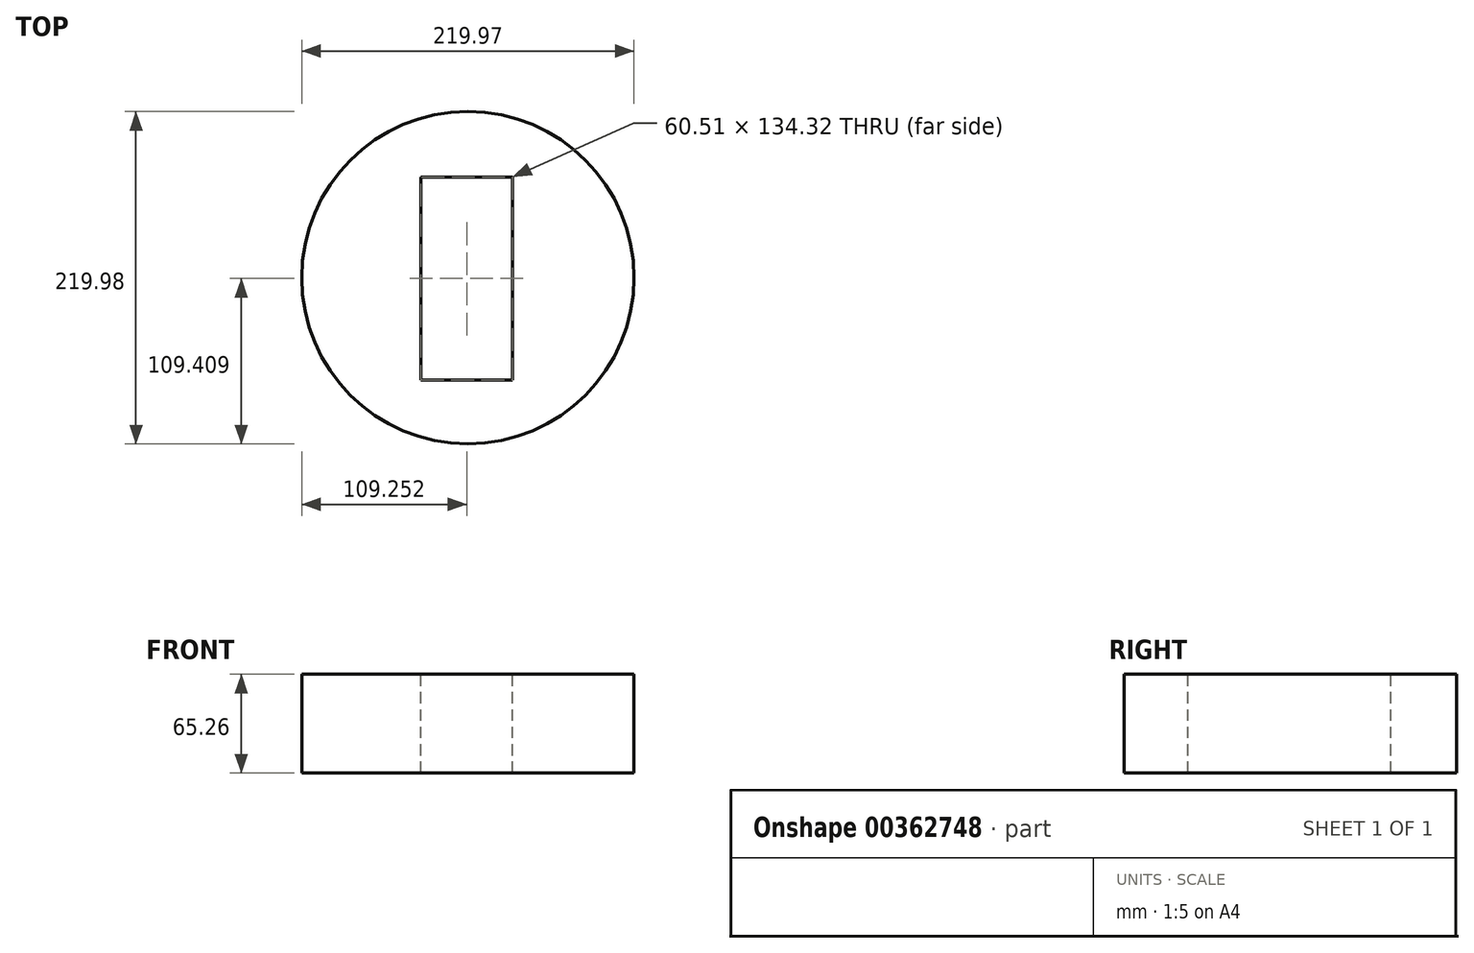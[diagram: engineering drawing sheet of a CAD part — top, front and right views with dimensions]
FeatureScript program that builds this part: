
annotation { "Feature Type Name" : "Feature", "Feature Type Description" : "" }
export const myFeature = defineFeature(function(context is Context, id is Id, definition is map)
    precondition{}
    {
        {
            var Q0;
            Q0=qCreatedBy(makeId("Front.planeOp"),FACE);
            var sketch = newSketch(context, id + "F0", { "sketchPlane" : qUnion([Q0])});
            skLineSegment(sketch, "E0", {"start": v(-7.15, 6.23) * mm, "end": v(-7.15, -67.46) * mm});
            skLineSegment(sketch, "E1.bottom", {"start": v(23.46, 0) * mm, "end": v(-86.52, 0) * mm});
            skLineSegment(sketch, "E1.top", {"start": v(23.46, 65.26) * mm, "end": v(-86.52, 65.26) * mm});
            skLineSegment(sketch, "E1.left", {"start": v(23.46, 0) * mm, "end": v(23.46, 65.26) * mm});
            skLineSegment(sketch, "E1.right", {"start": v(-86.52, 0) * mm, "end": v(-86.52, 65.26) * mm});
            skPoint(sketch, "E1.middle", {"position": v(-31.53, 32.63) * mm});
            skLineSegment(sketch, "E2.bottom", {"start": v(53.41, 64.58) * mm, "end": v(-6.49, 64.58) * mm, "construction": true});
            skLineSegment(sketch, "E2.top", {"start": v(53.41, 0.68) * mm, "end": v(-6.49, 0.68) * mm, "construction": true});
            skLineSegment(sketch, "E2.left", {"start": v(53.41, 64.58) * mm, "end": v(53.41, 0.68) * mm, "construction": true});
            skLineSegment(sketch, "E2.right", {"start": v(-6.49, 64.58) * mm, "end": v(-6.49, 0.68) * mm, "construction": true});
            skPoint(sketch, "E2.middle", {"position": v(23.46, 32.63) * mm});
            skLineSegment(sketch, "E3.bottom", {"start": v(77.4, 56.46) * mm, "end": v(93.99, 56.46) * mm, "construction": true});
            skLineSegment(sketch, "E3.top", {"start": v(77.4, 60.58) * mm, "end": v(93.99, 60.58) * mm, "construction": true});
            skLineSegment(sketch, "E3.left", {"start": v(77.4, 56.46) * mm, "end": v(77.4, 60.58) * mm, "construction": true});
            skLineSegment(sketch, "E3.right", {"start": v(93.99, 56.46) * mm, "end": v(93.99, 60.58) * mm, "construction": true});
            skPoint(sketch, "E3.middle", {"position": v(85.7, 58.52) * mm});
            skLineSegment(sketch, "E4.bottom", {"start": v(23.46, 0) * mm, "end": v(23.46, 0) * mm});
            skLineSegment(sketch, "E4.top", {"start": v(23.46, 91.65) * mm, "end": v(23.46, 91.65) * mm});
            skLineSegment(sketch, "E4.left", {"start": v(23.46, 0) * mm, "end": v(23.46, 91.65) * mm, "construction": true});
            skLineSegment(sketch, "E4.right", {"start": v(23.46, 0) * mm, "end": v(23.46, 91.65) * mm, "construction": true});
            skPoint(sketch, "E4.middle", {"position": v(23.46, 45.83) * mm});
            skLineSegment(sketch, "E5.bottom", {"start": v(-38.13, -61.96) * mm, "end": v(154.96, -61.96) * mm, "construction": true});
            skLineSegment(sketch, "E5.top", {"start": v(-38.13, 292.2) * mm, "end": v(154.96, 292.2) * mm, "construction": true});
            skLineSegment(sketch, "E5.left", {"start": v(-38.13, -61.96) * mm, "end": v(-38.13, 292.2) * mm, "construction": true});
            skLineSegment(sketch, "E5.right", {"start": v(154.96, -61.96) * mm, "end": v(154.96, 292.2) * mm, "construction": true});
            skPoint(sketch, "E5.middle", {"position": v(58.42, 115.12) * mm});
            skSolve(sketch);
        }
        {
            var Q0;
            Q0=makeQuery(id+"F0.imprint","IMPRINT",FACE,{"disambiguationData":[TD([[makeQuery(id+"F0.imprint","IMPRINT",EDGE,{"derivedFrom":sQuery(id+"F0.wireOp",EDGE,"E1.top")}),1.0]])]});
            var Q1;
            Q1=sQuery(id+"F0.wireOp",EDGE,"E1.right");
            revolve(context, id + "F1", {"entities" : qUnion([Q0]), "axis" : qUnion([Q1]), "revolveType" : RevolveType.FULL});
        }
        {
            var Q0;
            Q0=qCreatedBy(makeId("Top.planeOp"),FACE);
            var sketch = newSketch(context, id + "F2", { "sketchPlane" : qUnion([Q0])});
            skLineSegment(sketch, "E6.bottom", {"start": v(-60.15, 46.17) * mm, "end": v(-121.71, 46.17) * mm});
            skLineSegment(sketch, "E6.top", {"start": v(-60.15, -46.17) * mm, "end": v(-121.71, -46.17) * mm});
            skLineSegment(sketch, "E6.left", {"start": v(-60.15, 46.17) * mm, "end": v(-60.15, -46.17) * mm});
            skLineSegment(sketch, "E6.right", {"start": v(-121.71, 46.17) * mm, "end": v(-121.71, -46.17) * mm});
            skPoint(sketch, "E6.middle", {"position": v(-90.93, 0) * mm});
            skSolve(sketch);
        }
        {
            var Q0;
            Q0=sQuery(id+"F2.wireOp",VERTEX,"E6.middle");
            var Q1;
            Q1=makeQuery(id+"F1.opRevolve","SWEPT_BODY",BODY,{"disambiguationData":[OSD([sQuery(id+"F0.wireOp",EDGE,"E1.bottom"),sQuery(id+"F0.wireOp",EDGE,"E1.top"),sQuery(id+"F0.wireOp",EDGE,"E1.left"),sQuery(id+"F0.wireOp",EDGE,"E1.right")])]});
            hole(context, id + "F3", {"style" : HoleStyle.SIMPLE, "endStyle" : HoleEndStyle.THROUGH, "oppositeDirection" : true, "holeDiameter" : 6.35 * mm, "isTappedThrough" : true, "tappedDepth" : 12.7 * mm, "tapClearance" : 3, "locations" : qUnion([Q0]), "scope" : qUnion([Q1])});
        }
        {
            var Q0;
            Q0=makeQuery(id+"F1.opRevolve","SWEPT_FACE",FACE,{"disambiguationData":[OSD([sQuery(id+"F0.wireOp",EDGE,"E1.top")])]});
            var sketch = newSketch(context, id + "F4", { "sketchPlane" : qUnion([Q0])});
            skLineSegment(sketch, "E7.bottom", {"start": v(-117.51, 66.58) * mm, "end": v(-57, 66.58) * mm});
            skLineSegment(sketch, "E7.top", {"start": v(-117.51, -67.74) * mm, "end": v(-57, -67.74) * mm});
            skLineSegment(sketch, "E7.left", {"start": v(-117.51, 66.58) * mm, "end": v(-117.51, -67.74) * mm});
            skLineSegment(sketch, "E7.right", {"start": v(-57, 66.58) * mm, "end": v(-57, -67.74) * mm});
            skSolve(sketch);
        }
        {
            var Q0;
            Q0=makeQuery(id+"F4.imprint","IMPRINT",FACE,{"disambiguationData":[TD([[makeQuery(id+"F4.imprint","IMPRINT",EDGE,{"derivedFrom":sQuery(id+"F4.wireOp",EDGE,"E7.bottom")}),-1.0]])]});
            extrude(context, id + "F5", {"entities" : qUnion([Q0]), "operationType" : NewBodyOperationType.REMOVE, "endBound" : BoundingType.THROUGH_ALL, "oppositeDirection" : true, "depth" : 25.4 * mm});
        }
    });
